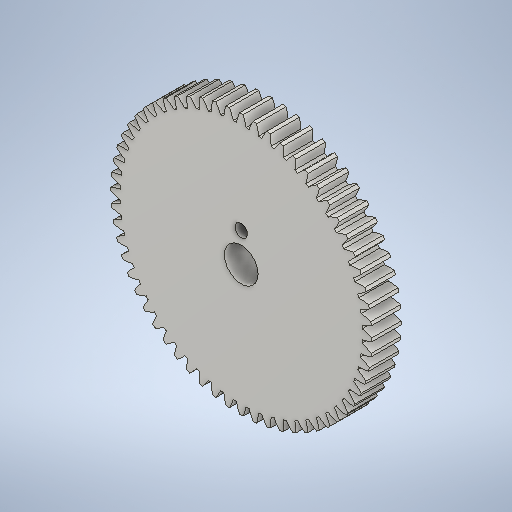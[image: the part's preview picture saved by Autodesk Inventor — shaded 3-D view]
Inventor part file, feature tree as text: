
AUTODESK INVENTOR PART (.ipt)
format: ipt  version: 2025.1 (Build 291241000, 241)  size: 521,216 bytes
history: native  units: mm (DEFAULTED — no unit token found)
features: sketch x4, extrude x3, plane x3, other x3
ambient origin geometry x8: Origin, YZ Plane, XZ Plane, XY Plane, X Axis, Y Axis, Z Axis, Center Point
bodies: Solid1 (feature_tree)
feature tree (13):
  extrude  "Extrusion1"  Depth=7.0mm TaperAngle=0.0deg
  plane  "Work Plane2"
  plane  "Work Plane8"
  plane  "Work Plane9"
  other  "Stirnzahnrad"
  extrude  "Extrusion2"  Depth=10.0mm TaperAngle=0.0deg
  extrude  "Extrusion3"  Depth=0.523599mm TaperAngle=0.0deg
  sketch  "Skizze4"  dims[d16=42.0mm d17=0.0mm d34=0.523599mm]
  sketch  "Sketch1"  dims[d0=62.0mm d1=7.0mm d2=0.0mm]
  other  "Srf1"
  sketch  "Skizze3"  dims[d3=60.0mm d4=10.0mm d5=0.0mm]
  sketch  "Skizze5"  dims[d39=0.0mm d41=0.0mm d43=42.0mm d46=42.0mm d47=0.0mm d48=0.0mm d49=8.0mm d50=10.0mm d51=0.0mm d52=60.0mm d53=7.0mm d54=3.0mm d55=10.0mm d56=0.0mm]
  other  "Flankendurchmesser"
